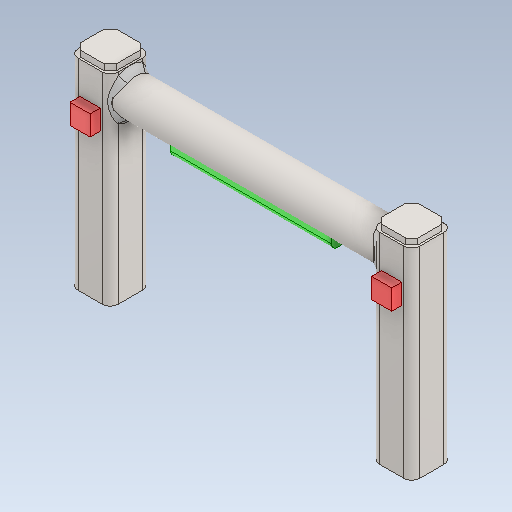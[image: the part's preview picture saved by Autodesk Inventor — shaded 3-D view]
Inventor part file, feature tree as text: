
AUTODESK INVENTOR PART (.ipt)
format: ipt  version: 2021 (Build 250183000, 183)  size: 268,800 bytes
history: mixed  units: mm
features: other x16, fillet x3, surface_op x1, imported_body x1
ambient origin geometry x8: Origin, YZ Plane, XZ Plane, XY Plane, X Axis, Y Axis, Z Axis, Center Point
bodies: Body1 (imported_parasolid), Body2 (imported_parasolid), Body3 (imported_parasolid), Body4 (imported_parasolid), Body5 (imported_parasolid), Body6 (imported_parasolid), Body7 (imported_parasolid), Body8 (imported_parasolid), Body9 (imported_parasolid), Body10 (imported_parasolid)
feature tree (21):
  other  "Sólido1"
  other  "Sólido2"
  other  "Sólido3"
  other  "Sólido4"
  other  "Sólido5"
  other  "Sólido6"
  other  "Sólido7"
  other  "Sólido8"
  other  "Sólido9"
  other  "Sólido10"
  other  "Structural Member4[2]"
  surface_op  "Trim_Extend5"
  fillet  "Fillet Bead4"  [1 undecoded]
  fillet  "Fillet Bead5"  [1 undecoded]
  other  "End cap2[1]"
  other  "End cap2[2]"
  other  "Boss-Extrude1"
  other  "LPattern1"
  fillet  "Fillet1"  [1 undecoded]
  other  "Boss-Extrude4"
  imported_body  NMx_Import_Brep_tag  [imported B-rep: ~23 faces, bbox_mm=None]
note: 3 required parameter values undecoded (feature->parameter linkage not recoverable at this tier; creation-order binding heuristic only, values carry confidence <= 0.55)
